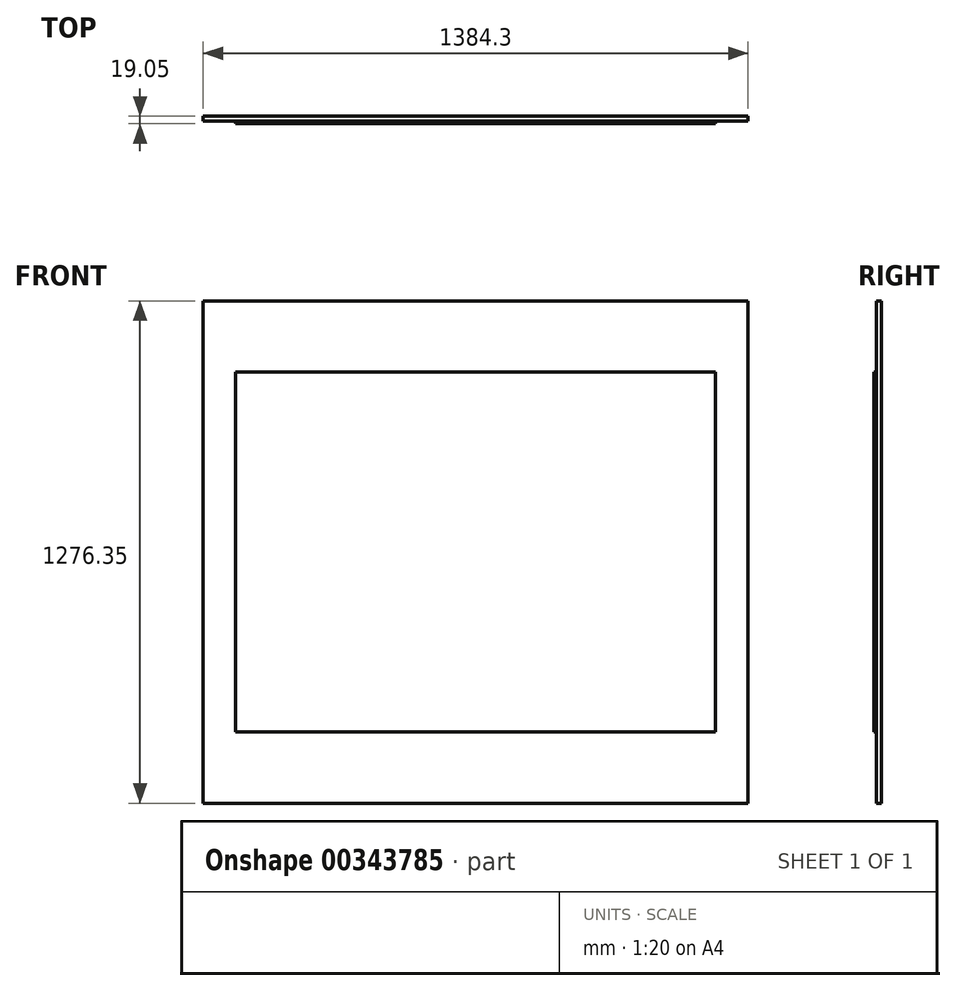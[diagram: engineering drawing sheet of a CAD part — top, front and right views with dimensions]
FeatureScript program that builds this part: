
annotation { "Feature Type Name" : "Feature", "Feature Type Description" : "" }
export const myFeature = defineFeature(function(context is Context, id is Id, definition is map)
    precondition{}
    {
        {
            var Q0;
            Q0=qCreatedBy(makeId("Front.planeOp"),FACE);
            var sketch = newSketch(context, id + "F0", { "sketchPlane" : qUnion([Q0])});
            skLineSegment(sketch, "E0.bottom", {"start": v(-700.64, 648.78) * mm, "end": v(683.66, 648.78) * mm});
            skLineSegment(sketch, "E0.top", {"start": v(-700.64, -627.57) * mm, "end": v(683.66, -627.57) * mm});
            skLineSegment(sketch, "E0.left", {"start": v(-700.64, 648.78) * mm, "end": v(-700.64, -627.57) * mm});
            skLineSegment(sketch, "E0.right", {"start": v(683.66, 648.78) * mm, "end": v(683.66, -627.57) * mm});
            skSolve(sketch);
        }
        {
            var Q0;
            Q0=makeQuery(id+"F0.imprint","IMPRINT",FACE,{"disambiguationData":[TD([[makeQuery(id+"F0.imprint","IMPRINT",EDGE,{"derivedFrom":sQuery(id+"F0.wireOp",EDGE,"E0.bottom")}),-1.0]])]});
            extrude(context, id + "F1", {"entities" : qUnion([Q0]), "oppositeDirection" : true, "depth" : 12.7 * mm});
        }
        {
            var Q0;
            Q0=makeQuery(id+"F1.opExtrude","CAP_FACE",FACE,{"disambiguationData":[OSD([sQuery(id+"F0.wireOp",EDGE,"E0.bottom"),sQuery(id+"F0.wireOp",EDGE,"E0.top"),sQuery(id+"F0.wireOp",EDGE,"E0.left"),sQuery(id+"F0.wireOp",EDGE,"E0.right")])],"isStart":true});
            var sketch = newSketch(context, id + "F2", { "sketchPlane" : qUnion([Q0])});
            skLineSegment(sketch, "E1.bottom", {"start": v(-618.09, 467.8) * mm, "end": v(601.11, 467.8) * mm});
            skLineSegment(sketch, "E1.top", {"start": v(-618.09, -446.6) * mm, "end": v(601.11, -446.6) * mm});
            skLineSegment(sketch, "E1.left", {"start": v(-618.09, 467.8) * mm, "end": v(-618.09, -446.6) * mm});
            skLineSegment(sketch, "E1.right", {"start": v(601.11, 467.8) * mm, "end": v(601.11, -446.6) * mm});
            skSolve(sketch);
        }
        {
            var Q0;
            Q0=makeQuery(id+"F2.imprint","IMPRINT",FACE,{"disambiguationData":[TD([[makeQuery(id+"F2.imprint","IMPRINT",EDGE,{"derivedFrom":sQuery(id+"F2.wireOp",EDGE,"E1.bottom")}),-1.0]])]});
            extrude(context, id + "F3", {"entities" : qUnion([Q0]), "depth" : 6.35 * mm});
        }
    });
